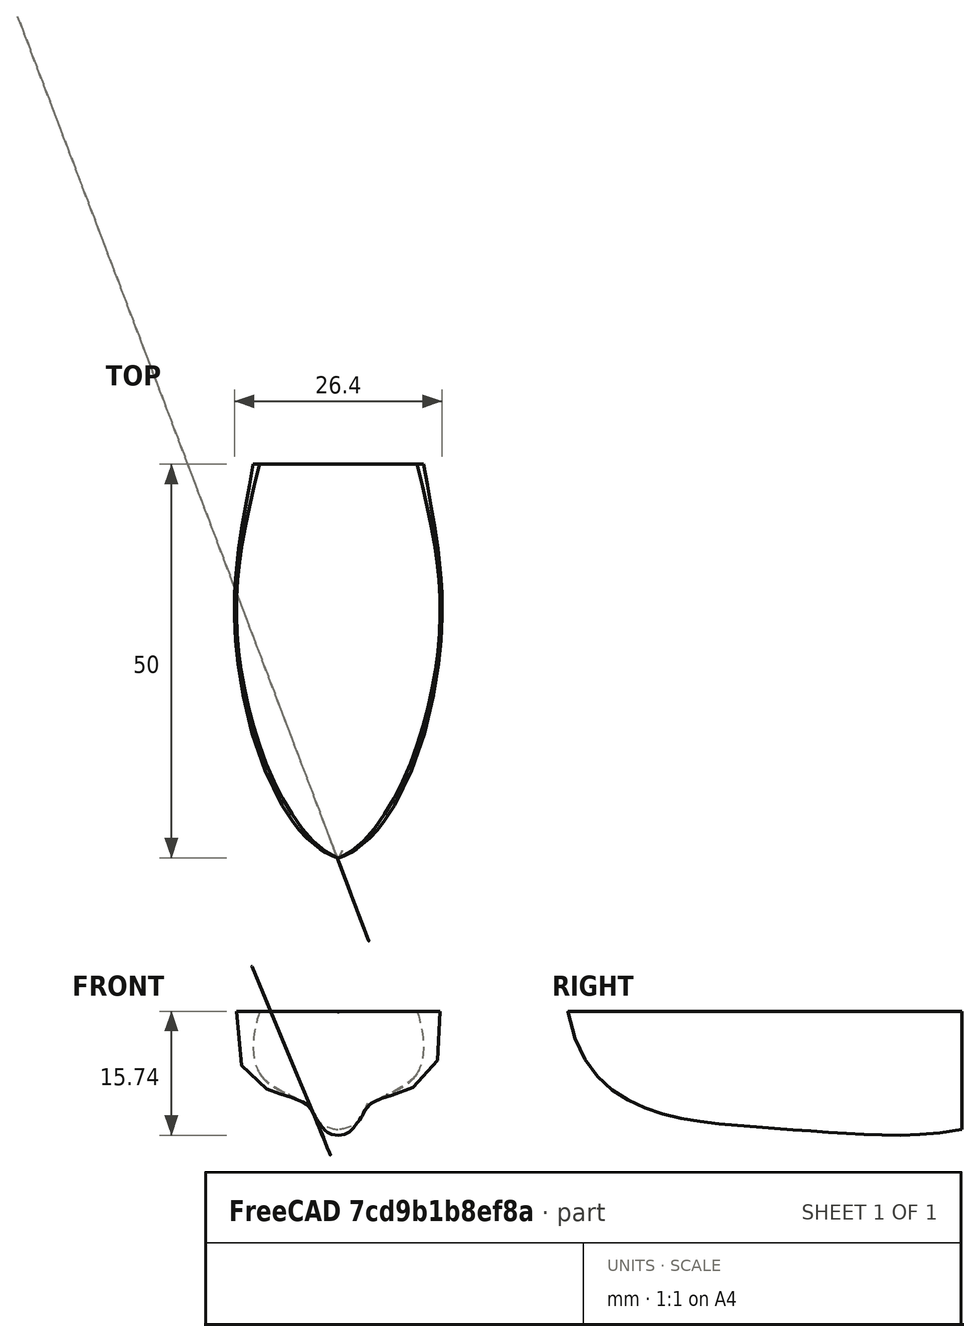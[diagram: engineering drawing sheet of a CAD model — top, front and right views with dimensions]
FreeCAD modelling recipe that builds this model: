
FCSTD DOCUMENT  (FreeCAD 1.0R38643 (Git))
Label: boat_loft
License: All rights reserved
LicenseURL: http://en.wikipedia.org/wiki/All_rights_reserved
objects: Sketcher::SketchObject×8, PartDesign::AdditiveLoft×1, PartDesign::Body×1
note: 20 computed .brp shape members not serialized (recipe doc carries the construction recipe); baked Part::Feature solids carry a one-line shape summary decoded from their .brp

FEATURE [Sketcher::SketchObject] Sketch  label="hull_stern"
  ArcFitTolerance = 1e-06
  AttachmentOffset = pos=(0,0,-25) rot=(0,0,1;0rad)
  AttachmentSupport = -> [XZ_Plane]
  FullyConstrained = false
  MakeInternals = false
  MapMode = 5
  Placement = pos=(0,25,-5.6e-15) rot=(1,0,0;1.5708rad)
  sketch-geometry (27):
    g0-g6: Circle [constr] x7 (B-spline internal-alignment scaffolding for g7; pole/knot coordinates omitted)
    g7: BSplineCurve PolesCount=7 KnotsCount=5 Degree=3 IsPeriodic=0
    g8-g12: GeomPoint [constr] x5 (B-spline internal-alignment scaffolding for g7; pole/knot coordinates omitted)
    g13-g19: Circle [constr] x7 (B-spline internal-alignment scaffolding for g20; pole/knot coordinates omitted)
    g20: BSplineCurve PolesCount=7 KnotsCount=5 Degree=3 IsPeriodic=0
    g21-g25: GeomPoint [constr] x5 (B-spline internal-alignment scaffolding for g20; pole/knot coordinates omitted)
    g26: LineSegment StartX=-10 StartY=0 StartZ=0 EndX=10 EndY=0 EndZ=0
  constraints (17):
    c: Weight(g0) = 1
    c: Equal(g0, g1-g6) x6
    c: InternalAlignment(g0-g6 -> g7) x7
    c: InternalAlignment(g8-g12 -> g7) x5
    c: PointOnObject(g0,g-1)
    c: Horizontal(g5,g7)
    c: DistanceX(g7,g-1) = 10
    c: DistanceY(g7,g-1) = 15
    c: Weight(g13) = 1
    c: Equal(g13, g14-g19) x6
    c: InternalAlignment(g13-g19 -> g20) x7
    c: InternalAlignment(g21-g25 -> g20) x5
    c: Coincident(g26,g7)
    c: Coincident(g26,g20)
    c: Horizontal(g26)
    c: PointOnObject(g7,g-2)
    c: Coincident(g20,g7)
FEATURE [Sketcher::SketchObject] Sketch001  label="hull_bow"
  ArcFitTolerance = 1e-06
  AttachmentOffset = pos=(0,0,25) rot=(0,0,1;0rad)
  AttachmentSupport = -> [XZ_Plane]
  FullyConstrained = true
  MakeInternals = false
  MapMode = 5
  Placement = pos=(0,-25,5.6e-15) rot=(1,0,0;1.5708rad)
  sketch-geometry (2):
    g0: ArcOfCircle CenterX=0 CenterY=0 CenterZ=0 NormalX=0 NormalY=0 NormalZ=1 AngleXU=0 Radius=0.1 StartAngle=3.14159 EndAngle=6.28319
    g1: LineSegment StartX=-0.1 StartY=0 StartZ=0 EndX=0.1 EndY=0 EndZ=0
  constraints (6):
    c: PointOnObject(g0,g-1)
    c: PointOnObject(g0,g-1)
    c: Coincident(g0,g-1)
    c: Radius(g0) = 0.1
    c: Coincident(g1,g0)
    c: Coincident(g1,g0)
FEATURE [Sketcher::SketchObject] Sketch002  label="hull_xy"
  ArcFitTolerance = 1e-06
  AttachmentSupport = -> [XY_Plane]
  ExternalGeometry = -> [Sketch,Sketch001]
  FullyConstrained = false
  MakeInternals = false
  MapMode = 5
  sketch-geometry (18):
    g0: Circle [constr] CenterX=-10 CenterY=25 CenterZ=0 NormalX=0 NormalY=0 NormalZ=1 AngleXU=0 Radius=1
    g1: Circle [constr] CenterX=-0.1 CenterY=-25 CenterZ=0 NormalX=0 NormalY=0 NormalZ=1 AngleXU=0 Radius=1
    g2: BSplineCurve PolesCount=5 KnotsCount=3 Degree=3 IsPeriodic=0
    g3: GeomPoint [constr] X=-10 Y=25 Z=0
    g4: GeomPoint [constr] X=-0.1 Y=-25 Z=0
    g5: Circle [constr] CenterX=-13.5323 CenterY=16.2252 CenterZ=0 NormalX=0 NormalY=0 NormalZ=1 AngleXU=0 Radius=1
    g6: Circle [constr] CenterX=-14.5076 CenterY=-7.35803 CenterZ=0 NormalX=0 NormalY=0 NormalZ=1 AngleXU=0 Radius=1
    g7: Circle [constr] CenterX=-3.22709 CenterY=-25 CenterZ=0 NormalX=0 NormalY=0 NormalZ=1 AngleXU=0 Radius=1
    g8: GeomPoint [constr] X=-11.2664 Y=-6.56607 Z=0
    g9: Circle [constr] CenterX=10 CenterY=25 CenterZ=0 NormalX=0 NormalY=0 NormalZ=1 AngleXU=0 Radius=1
    g10: BSplineCurve PolesCount=5 KnotsCount=3 Degree=3 IsPeriodic=0
    g11: GeomPoint [constr] X=10 Y=25 Z=0
    g12: GeomPoint [constr] X=0.1 Y=-25 Z=0
    g13: Circle [constr] CenterX=13.5323 CenterY=16.2252 CenterZ=0 NormalX=0 NormalY=0 NormalZ=1 AngleXU=0 Radius=1
    g14: Circle [constr] CenterX=14.5076 CenterY=-7.35803 CenterZ=0 NormalX=0 NormalY=0 NormalZ=1 AngleXU=0 Radius=1
    g15: Circle [constr] CenterX=3.22709 CenterY=-25 CenterZ=0 NormalX=0 NormalY=0 NormalZ=1 AngleXU=0 Radius=1
    g16: GeomPoint [constr] X=11.2664 Y=-6.56607 Z=0
    g17: Circle [constr] CenterX=0.1 CenterY=-25 CenterZ=0 NormalX=0 NormalY=0 NormalZ=1 AngleXU=0 Radius=1
  constraints (29):
    c: Weight(g0) = 1
    c: Equal(g0,g1)
    c: InternalAlignment(g0,g2)
    c: InternalAlignment(g1,g2)
    c: InternalAlignment(g3,g2)
    c: InternalAlignment(g4,g2)
    c: Coincident(g0,g-3)
    c: Coincident(g1,g-4)
    c: InternalAlignment(g5,g2)
    c: Equal(g5,g0)
    c: InternalAlignment(g6,g2)
    c: Equal(g6,g0)
    c: InternalAlignment(g7,g2)
    c: Equal(g7,g0)
    c: InternalAlignment(g8,g2)
    c: Horizontal(g7,g2)
    c: Weight(g9) = 1
    c: Equal(g9,g17)
    c: InternalAlignment(g9,g10)
    c: InternalAlignment(g17,g10)
    c: InternalAlignment(g11,g10)
    c: InternalAlignment(g12,g10)
    c: InternalAlignment(g13,g10)
    c: Equal(g13,g9)
    c: InternalAlignment(g14,g10)
    c: Equal(g14,g9)
    c: InternalAlignment(g15,g10)
    c: Equal(g15,g9)
    c: InternalAlignment(g16,g10)
FEATURE [Sketcher::SketchObject] Sketch003  label="hull_yz"
  ArcFitTolerance = 1e-06
  AttachmentSupport = -> [YZ_Plane]
  ExternalGeometry = -> [Sketch001,Sketch]
  FullyConstrained = true
  MakeInternals = false
  MapMode = 5
  Placement = pos=(0,0,0) rot=(0.57735,0.57735,0.57735;2.0944rad)
  sketch-geometry (8):
    g0-g3: Circle [constr] x4 (B-spline internal-alignment scaffolding for g4; pole/knot coordinates omitted)
    g4: BSplineCurve PolesCount=4 KnotsCount=2 Degree=3 IsPeriodic=0
    g5: GeomPoint [constr] X=-25 Y=-0.1 Z=0
    g6: GeomPoint [constr] X=3 Y=-15 Z=0
    g7: LineSegment StartX=3 StartY=-15 StartZ=0 EndX=25 EndY=-15 EndZ=0
  constraints (15):
    c: Weight(g0) = 1
    c: Equal(g0,g1)
    c: Equal(g0,g2)
    c: Equal(g0,g3)
    c: InternalAlignment(g0-g3 -> g4) x4
    c: InternalAlignment(g5,g4)
    c: InternalAlignment(g6,g4)
    c: Coincident(g0,g-3)
    c: Coincident(g7,g-4)
    c: Horizontal(g7)
    c: Tangent(g4,g7) = -1.5708
    c: Vertical(g4,g1)
    c: DistanceY(g1,g4) = 4
    c: Distance(g2,g-2) = 22
    c: DistanceX(g7,g7) = 22
FEATURE [Sketcher::SketchObject] Sketch004  label="hull_stern001"
  ArcFitTolerance = 1e-06
  AttachmentOffset = pos=(0,0,-3) rot=(0,0,1;0rad)
  AttachmentSupport = -> [XZ_Plane]
  FullyConstrained = false
  MakeInternals = false
  MapMode = 5
  Placement = pos=(0,3,-7e-16) rot=(1,0,0;1.5708rad)
  sketch-geometry (27):
    g0-g6: Circle [constr] x7 (B-spline internal-alignment scaffolding for g7; pole/knot coordinates omitted)
    g7: BSplineCurve PolesCount=7 KnotsCount=5 Degree=3 IsPeriodic=0
    g8-g12: GeomPoint [constr] x5 (B-spline internal-alignment scaffolding for g7; pole/knot coordinates omitted)
    g13: LineSegment StartX=-12.8116 StartY=0 StartZ=0 EndX=12.8116 EndY=0 EndZ=0
    g14-g17: Circle [constr] x4 (B-spline internal-alignment scaffolding for g18; pole/knot coordinates omitted)
    g18: BSplineCurve PolesCount=7 KnotsCount=5 Degree=3 IsPeriodic=0
    g19-g23: GeomPoint [constr] x5 (B-spline internal-alignment scaffolding for g18; pole/knot coordinates omitted)
    g24: Circle [constr] CenterX=14.3182 CenterY=-8.87642 CenterZ=0 NormalX=0 NormalY=0 NormalZ=1 AngleXU=0 Radius=1
    g25: Circle [constr] CenterX=0.607617 CenterY=-15 CenterZ=0 NormalX=0 NormalY=0 NormalZ=1 AngleXU=0 Radius=1
    g26: Circle [constr] CenterX=0 CenterY=-15 CenterZ=0 NormalX=0 NormalY=0 NormalZ=1 AngleXU=0 Radius=1
  constraints (27):
    c: Weight(g0) = 1
    c: Equal(g0, g1-g6) x6
    c: InternalAlignment(g0-g6 -> g7) x7
    c: InternalAlignment(g8-g12 -> g7) x5
    c: PointOnObject(g0,g-1)
    c: Horizontal(g5,g7)
    c: DistanceY(g7,g-1) = 15
    c: Coincident(g13,g7)
    c: Horizontal(g13)
    c: Weight(g14) = 1
    c: Equal(g14,g24)
    c: Equal(g14,g15)
    c: Equal(g14,g16)
    c: Equal(g14,g17)
    c: Equal(g14,g25)
    c: Equal(g14,g26)
    c: InternalAlignment(g14,g18)
    c: InternalAlignment(g24,g18)
    c: InternalAlignment(g15,g18)
    c: InternalAlignment(g16,g18)
    c: InternalAlignment(g17,g18)
    c: InternalAlignment(g25,g18)
    c: InternalAlignment(g26,g18)
    c: InternalAlignment(g19-g23 -> g18) x5
    c: Coincident(g13,g18)
    c: PointOnObject(g7,g-2)
    c: Coincident(g18,g7)
FEATURE [Sketcher::SketchObject] Sketch005  label="hull_stern002"
  ArcFitTolerance = 1e-06
  AttachmentOffset = pos=(0,0,10) rot=(0,0,1;0rad)
  AttachmentSupport = -> [XZ_Plane]
  FullyConstrained = false
  MakeInternals = false
  MapMode = 5
  Placement = pos=(0,-10,2.2e-15) rot=(1,0,0;1.5708rad)
  sketch-geometry (27):
    g0-g6: Circle [constr] x7 (B-spline internal-alignment scaffolding for g7; pole/knot coordinates omitted)
    g7: BSplineCurve PolesCount=7 KnotsCount=5 Degree=3 IsPeriodic=0
    g8-g12: GeomPoint [constr] x5 (B-spline internal-alignment scaffolding for g7; pole/knot coordinates omitted)
    g13: BSplineCurve PolesCount=7 KnotsCount=5 Degree=3 IsPeriodic=0
    g14-g20: Circle [constr] x7 (B-spline internal-alignment scaffolding for g13; pole/knot coordinates omitted)
    g21-g25: GeomPoint [constr] x5 (B-spline internal-alignment scaffolding for g13; pole/knot coordinates omitted)
    g26: LineSegment StartX=-10.2292 StartY=0 StartZ=0 EndX=10.2292 EndY=0 EndZ=0
  constraints (14):
    c: Weight(g0) = 1
    c: Equal(g0, g1-g6) x6
    c: InternalAlignment(g0-g6 -> g7) x7
    c: InternalAlignment(g8-g12 -> g7) x5
    c: PointOnObject(g0,g-1)
    c: Horizontal(g5,g7)
    c: PointOnObject(g7,g-2)
    c: Weight(g14) = 1
    c: Equal(g14, g15-g20) x6
    c: InternalAlignment(g14-g25 -> g13) x12
    c: Coincident(g26,g7)
    c: Coincident(g26,g13)
    c: Horizontal(g26)
    c: Coincident(g7,g13)
FEATURE [Sketcher::SketchObject] Sketch006  label="hull_stern003"
  ArcFitTolerance = 1e-06
  AttachmentOffset = pos=(0,0,20) rot=(0,0,1;0rad)
  AttachmentSupport = -> [XZ_Plane]
  FullyConstrained = false
  MakeInternals = false
  MapMode = 5
  Placement = pos=(0,-20,4.4e-15) rot=(1,0,0;1.5708rad)
  sketch-geometry (27):
    g0-g6: Circle [constr] x7 (B-spline internal-alignment scaffolding for g7; pole/knot coordinates omitted)
    g7: BSplineCurve PolesCount=7 KnotsCount=5 Degree=3 IsPeriodic=0
    g8-g12: GeomPoint [constr] x5 (B-spline internal-alignment scaffolding for g7; pole/knot coordinates omitted)
    g13-g16: Circle [constr] x4 (B-spline internal-alignment scaffolding for g17; pole/knot coordinates omitted)
    g17: BSplineCurve PolesCount=7 KnotsCount=5 Degree=3 IsPeriodic=0
    g18-g22: GeomPoint [constr] x5 (B-spline internal-alignment scaffolding for g17; pole/knot coordinates omitted)
    g23: Circle [constr] CenterX=7.12251 CenterY=-4.94554 CenterZ=0 NormalX=0 NormalY=0 NormalZ=1 AngleXU=0 Radius=1
    g24: Circle [constr] CenterX=1.08995 CenterY=-9.50094 CenterZ=0 NormalX=0 NormalY=0 NormalZ=1 AngleXU=0 Radius=1
    g25: Circle [constr] CenterX=0 CenterY=-9.50094 CenterZ=0 NormalX=0 NormalY=0 NormalZ=1 AngleXU=0 Radius=1
    g26: LineSegment StartX=-5.52841 StartY=0 StartZ=0 EndX=5.52841 EndY=0 EndZ=0
  constraints (26):
    c: Weight(g0) = 1
    c: Equal(g0, g1-g6) x6
    c: InternalAlignment(g0-g6 -> g7) x7
    c: InternalAlignment(g8-g12 -> g7) x5
    c: PointOnObject(g0,g-1)
    c: Horizontal(g5,g7)
    c: PointOnObject(g7,g-2)
    c: Weight(g13) = 1
    c: Equal(g13,g23)
    c: Equal(g13,g14)
    c: Equal(g13,g15)
    c: Equal(g13,g16)
    c: Equal(g13,g24)
    c: Equal(g13,g25)
    c: InternalAlignment(g13,g17)
    c: InternalAlignment(g23,g17)
    c: InternalAlignment(g14,g17)
    c: InternalAlignment(g15,g17)
    c: InternalAlignment(g16,g17)
    c: InternalAlignment(g24,g17)
    c: InternalAlignment(g25,g17)
    c: InternalAlignment(g18-g22 -> g17) x5
    c: Coincident(g26,g7)
    c: Coincident(g26,g17)
    c: Horizontal(g26)
    c: Coincident(g7,g17)
FEATURE [Sketcher::SketchObject] Sketch007  label="hull_stern004"
  ArcFitTolerance = 1e-06
  AttachmentOffset = pos=(0,0,25) rot=(0,0,1;0rad)
  AttachmentSupport = -> [XZ_Plane]
  FullyConstrained = false
  MakeInternals = false
  MapMode = 5
  Placement = pos=(0,-25,5.6e-15) rot=(1,0,0;1.5708rad)
  sketch-geometry (27):
    g0-g6: Circle [constr] x7 (B-spline internal-alignment scaffolding for g7; pole/knot coordinates omitted)
    g7: BSplineCurve PolesCount=7 KnotsCount=5 Degree=3 IsPeriodic=0
    g8-g12: GeomPoint [constr] x5 (B-spline internal-alignment scaffolding for g7; pole/knot coordinates omitted)
    g13: BSplineCurve PolesCount=7 KnotsCount=5 Degree=3 IsPeriodic=0
    g14-g20: Circle [constr] x7 (B-spline internal-alignment scaffolding for g13; pole/knot coordinates omitted)
    g21-g25: GeomPoint [constr] x5 (B-spline internal-alignment scaffolding for g13; pole/knot coordinates omitted)
    g26: LineSegment StartX=-0.101026 StartY=0 StartZ=0 EndX=0.101026 EndY=0 EndZ=0
  constraints (14):
    c: Weight(g0) = 1
    c: Equal(g0, g1-g6) x6
    c: InternalAlignment(g0-g6 -> g7) x7
    c: InternalAlignment(g8-g12 -> g7) x5
    c: PointOnObject(g0,g-1)
    c: PointOnObject(g6,g-2)
    c: Horizontal(g5,g7)
    c: Weight(g14) = 1
    c: Equal(g14, g15-g20) x6
    c: InternalAlignment(g14-g25 -> g13) x12
    c: Coincident(g26,g7)
    c: Coincident(g26,g13)
    c: Horizontal(g26)
    c: Coincident(g7,g13)
FEATURE [PartDesign::AdditiveLoft] AdditiveLoft
  Closed = false
  Placement = pos=(0,0,0) rot=(1,0,0;1.5708rad)
  Profile = -> Sketch
  Ruled = false
  Sections = -> [Sketch004,Sketch005,Sketch006,Sketch007]
  Suppressed = false
FEATURE [PartDesign::Body] Body
  AllowCompound = false
  Group = -> [Sketch,Sketch001,Sketch002,Sketch003,Sketch004,Sketch005,Sketch006,Sketch007,AdditiveLoft]
  Origin = -> Origin
  Tip = -> AdditiveLoft
